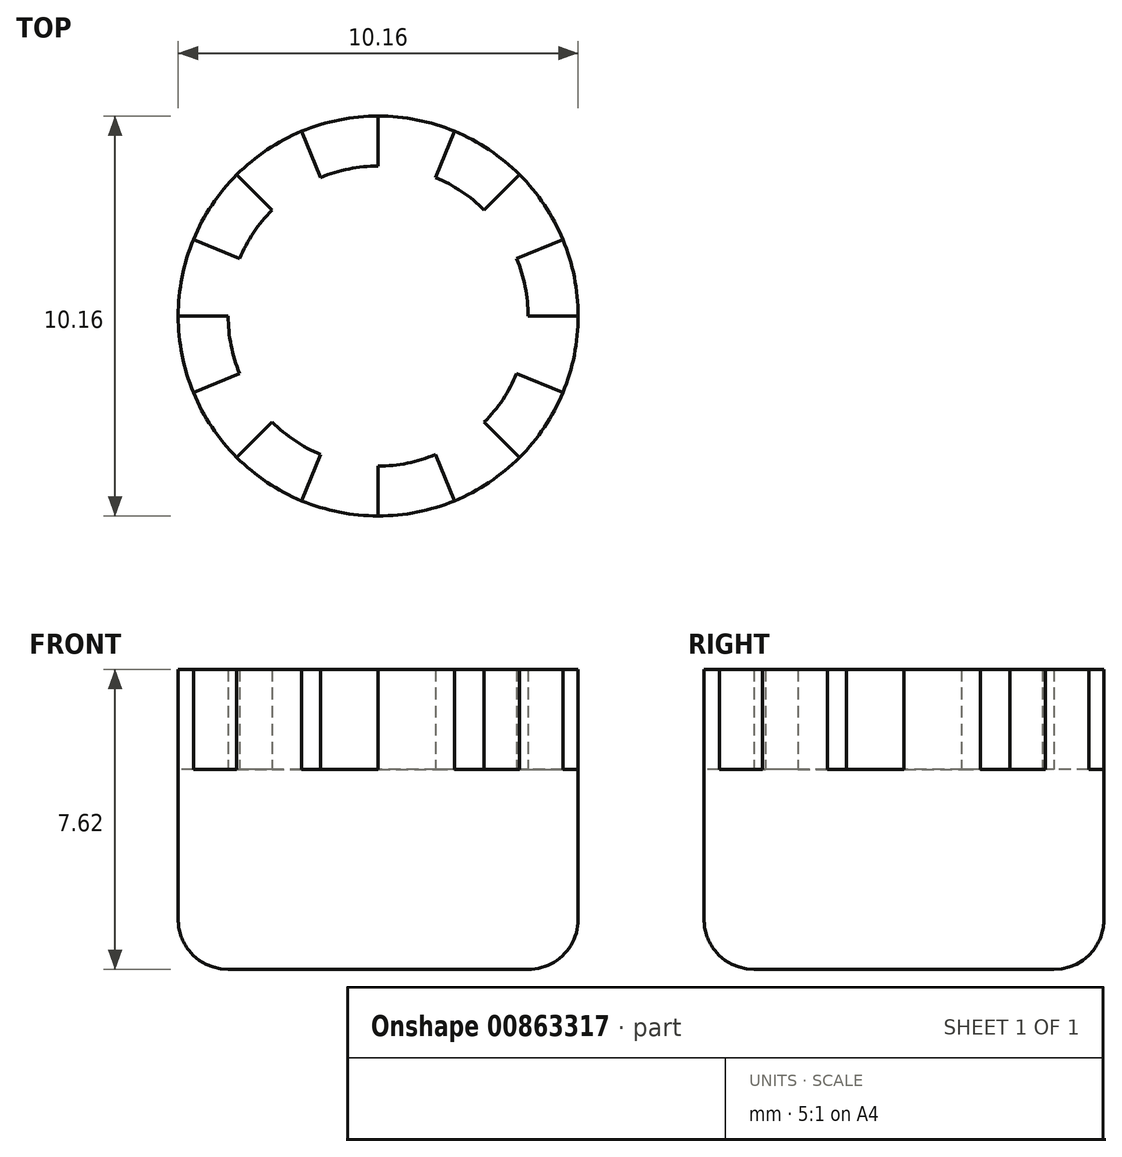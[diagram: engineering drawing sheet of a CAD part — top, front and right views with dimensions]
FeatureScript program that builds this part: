
annotation { "Feature Type Name" : "Feature", "Feature Type Description" : "" }
export const myFeature = defineFeature(function(context is Context, id is Id, definition is map)
    precondition{}
    {
        {
            var Q0;
            Q0=qCreatedBy(makeId("Top.planeOp"),FACE);
            var sketch = newSketch(context, id + "F0", { "sketchPlane" : qUnion([Q0])});
            skCircle(sketch, "E0", {"center": v(0, 0) * mm, "radius": 5.08 * mm});
            skArc(sketch, "E1", {"start": v(0, 3.81) * mm, "mid": v(-0.74, 3.74) * mm, "end": v(-1.46, 3.52) * mm});
            skLineSegment(sketch, "E2", {"start": v(-5.08, 0) * mm, "end": v(-3.81, 0) * mm});
            skLineSegment(sketch, "E3", {"start": v(0, 5.08) * mm, "end": v(0, 3.81) * mm});
            skLineSegment(sketch, "E4", {"start": v(-3.6, 3.6) * mm, "end": v(-2.7, 2.7) * mm});
            skLineSegment(sketch, "E5", {"start": v(2.7, -2.7) * mm, "end": v(3.6, -3.6) * mm});
            skLineSegment(sketch, "E6", {"start": v(-1.94, 4.7) * mm, "end": v(-1.46, 3.52) * mm});
            skLineSegment(sketch, "E7", {"start": v(1.46, -3.52) * mm, "end": v(1.94, -4.7) * mm});
            skLineSegment(sketch, "E8", {"start": v(-3.52, 1.46) * mm, "end": v(-4.7, 1.94) * mm});
            skLineSegment(sketch, "E9", {"start": v(3.52, -1.46) * mm, "end": v(4.7, -1.94) * mm});
            skLineSegment(sketch, "E10", {"start": v(1.46, 3.52) * mm, "end": v(1.94, 4.7) * mm});
            skLineSegment(sketch, "E11", {"start": v(2.7, 2.7) * mm, "end": v(3.6, 3.6) * mm});
            skLineSegment(sketch, "E12", {"start": v(3.52, 1.46) * mm, "end": v(4.7, 1.94) * mm});
            skLineSegment(sketch, "E13", {"start": v(-2.7, -2.7) * mm, "end": v(-3.6, -3.6) * mm});
            skLineSegment(sketch, "E14", {"start": v(-3.52, -1.46) * mm, "end": v(-4.7, -1.94) * mm});
            skLineSegment(sketch, "E15", {"start": v(-1.46, -3.52) * mm, "end": v(-1.94, -4.7) * mm});
            skLineSegment(sketch, "E16.trimOffspring", {"start": v(0, -3.81) * mm, "end": v(0, -5.08) * mm});
            skLineSegment(sketch, "E17.trimOffspring", {"start": v(3.81, 0) * mm, "end": v(5.08, 0) * mm});
            skArc(sketch, "E18.trimOffspring", {"start": v(-2.7, 2.7) * mm, "mid": v(-3.17, 2.12) * mm, "end": v(-3.52, 1.46) * mm});
            skArc(sketch, "E19.trimOffspring", {"start": v(2.7, 2.7) * mm, "mid": v(2.12, 3.17) * mm, "end": v(1.46, 3.52) * mm});
            skArc(sketch, "E20.trimOffspring", {"start": v(3.81, 0) * mm, "mid": v(3.74, 0.74) * mm, "end": v(3.52, 1.46) * mm});
            skArc(sketch, "E21.trimOffspring", {"start": v(2.7, -2.7) * mm, "mid": v(3.17, -2.12) * mm, "end": v(3.52, -1.46) * mm});
            skArc(sketch, "E22.trimOffspring", {"start": v(0, -3.81) * mm, "mid": v(0.74, -3.74) * mm, "end": v(1.46, -3.52) * mm});
            skArc(sketch, "E23.trimOffspring", {"start": v(-2.7, -2.7) * mm, "mid": v(-2.12, -3.17) * mm, "end": v(-1.46, -3.52) * mm});
            skArc(sketch, "E24.trimOffspring", {"start": v(-3.81, 0) * mm, "mid": v(-3.74, -0.74) * mm, "end": v(-3.52, -1.46) * mm});
            skSolve(sketch);
        }
        {
            var Q0;
            Q0=makeQuery(id+"F0.imprint","IMPRINT",FACE,{"disambiguationData":[TD([[makeQuery(id+"F0.imprint","IMPRINT",EDGE,{"derivedFrom":sQuery(id+"F0.wireOp",EDGE,"E1")}),1.0]])]});
            extrude(context, id + "F1", {"entities" : qUnion([Q0]), "depth" : 5.08 * mm, "offsetDistance" : 25.4 * mm});
        }
        {
            var Q0;
            Q0=makeQuery(id+"F0.imprint","IMPRINT",FACE,{"disambiguationData":[TD([[makeQuery(id+"F0.imprint","IMPRINT",EDGE,{"derivedFrom":sQuery(id+"F0.wireOp",EDGE,"E1")}),-1.0]])]});
            var Q1;
            {var subQ0=sQuery(id+"F0.wireOp",EDGE,"E10");Q1=makeQuery(id+"F0.imprint","IMPRINT",FACE,{"disambiguationData":[TD([[makeQuery(id+"F0.imprint","IMPRINT",EDGE,{"derivedFrom":subQ0}),-1.0]])]});}
            var Q2;
            {var subQ0=sQuery(id+"F0.wireOp",EDGE,"E12");Q2=makeQuery(id+"F0.imprint","IMPRINT",FACE,{"disambiguationData":[TD([[makeQuery(id+"F0.imprint","IMPRINT",EDGE,{"derivedFrom":subQ0}),-1.0]])]});}
            var Q3;
            {var subQ0=sQuery(id+"F0.wireOp",EDGE,"E4");Q3=makeQuery(id+"F0.imprint","IMPRINT",FACE,{"disambiguationData":[TD([[makeQuery(id+"F0.imprint","IMPRINT",EDGE,{"derivedFrom":subQ0}),-1.0]])]});}
            var Q4;
            {var subQ0=sQuery(id+"F0.wireOp",EDGE,"E2");Q4=makeQuery(id+"F0.imprint","IMPRINT",FACE,{"disambiguationData":[TD([[makeQuery(id+"F0.imprint","IMPRINT",EDGE,{"derivedFrom":subQ0}),-1.0]])]});}
            var Q5;
            {var subQ0=sQuery(id+"F0.wireOp",EDGE,"E13");Q5=makeQuery(id+"F0.imprint","IMPRINT",FACE,{"disambiguationData":[TD([[makeQuery(id+"F0.imprint","IMPRINT",EDGE,{"derivedFrom":subQ0}),1.0]])]});}
            var Q6;
            {var subQ0=sQuery(id+"F0.wireOp",EDGE,"E7");Q6=makeQuery(id+"F0.imprint","IMPRINT",FACE,{"disambiguationData":[TD([[makeQuery(id+"F0.imprint","IMPRINT",EDGE,{"derivedFrom":subQ0}),-1.0]])]});}
            var Q7;
            {var subQ0=sQuery(id+"F0.wireOp",EDGE,"E5");Q7=makeQuery(id+"F0.imprint","IMPRINT",FACE,{"disambiguationData":[TD([[makeQuery(id+"F0.imprint","IMPRINT",EDGE,{"derivedFrom":subQ0}),1.0]])]});}
            extrude(context, id + "F2", {"entities" : qUnion([Q0, Q1, Q2, Q3, Q4, Q5, Q6, Q7]), "operationType" : NewBodyOperationType.ADD, "depth" : 7.62 * mm, "offsetDistance" : 25.4 * mm});
        }
        {
            var Q0;
            {var subQ0=sQuery(id+"F0.wireOp",EDGE,"E0");var subQ1=makeQuery(id+"F0.imprint","INTERSECT",VERTEX,{"derivedFrom":[subQ0,sQuery(id+"F0.wireOp",EDGE,"E5")]});var subQ2=makeQuery(id+"F0.imprint","INTERSECT",VERTEX,{"derivedFrom":[subQ0,sQuery(id+"F0.wireOp",EDGE,"E9")]});var subQ3=makeQuery(id+"F0.imprint","INTERSECT",VERTEX,{"derivedFrom":[subQ0,sQuery(id+"F0.wireOp",EDGE,"E7")]});var subQ5=makeQuery(id+"F0.imprint","INTERSECT",VERTEX,{"derivedFrom":[subQ0,sQuery(id+"F0.wireOp",EDGE,"E13")]});var subQ6=makeQuery(id+"F0.imprint","INTERSECT",VERTEX,{"derivedFrom":[subQ0,sQuery(id+"F0.wireOp",EDGE,"E15")]});var subQ7=makeQuery(id+"F0.imprint","INTERSECT",VERTEX,{"derivedFrom":[subQ0,sQuery(id+"F0.wireOp",EDGE,"E2")]});var subQ9=makeQuery(id+"F0.imprint","INTERSECT",VERTEX,{"derivedFrom":[subQ0,sQuery(id+"F0.wireOp",EDGE,"E4")]});var subQ11=makeQuery(id+"F0.imprint","INTERSECT",VERTEX,{"derivedFrom":[subQ0,sQuery(id+"F0.wireOp",EDGE,"E3")]});var subQ13=makeQuery(id+"F0.imprint","INTERSECT",VERTEX,{"derivedFrom":[subQ0,sQuery(id+"F0.wireOp",EDGE,"E10")]});var subQ14=makeQuery(id+"F0.imprint","INTERSECT",VERTEX,{"derivedFrom":[subQ0,sQuery(id+"F0.wireOp",EDGE,"E11")]});var subQ15=makeQuery(id+"F0.imprint","INTERSECT",VERTEX,{"derivedFrom":[subQ0,sQuery(id+"F0.wireOp",EDGE,"E12")]});Q0=makeQuery(id+"F2.boolean.opBoolean","MERGE",EDGE,{"derivedFrom":[makeQuery(id+"F1.opExtrude","CAP_EDGE",EDGE,{"disambiguationData":[OSD([subQ0]),TDD([makeQuery(id+"F0.imprint","IMPRINT",EDGE,{"disambiguationData":[TD([[subQ14,1.0]])],"derivedFrom":subQ0})])],"isStart":true}),makeQuery(id+"F1.opExtrude","CAP_EDGE",EDGE,{"disambiguationData":[OSD([subQ0]),TDD([makeQuery(id+"F0.imprint","IMPRINT",EDGE,{"disambiguationData":[TD([[subQ11,1.0]])],"derivedFrom":subQ0})])],"isStart":true}),makeQuery(id+"F1.opExtrude","CAP_EDGE",EDGE,{"disambiguationData":[OSD([subQ0]),TDD([makeQuery(id+"F0.imprint","IMPRINT",EDGE,{"disambiguationData":[TD([[subQ9,1.0]])],"derivedFrom":subQ0})])],"isStart":true}),makeQuery(id+"F1.opExtrude","CAP_EDGE",EDGE,{"disambiguationData":[OSD([subQ0]),TDD([makeQuery(id+"F0.imprint","IMPRINT",EDGE,{"disambiguationData":[TD([[subQ7,1.0]])],"derivedFrom":subQ0})])],"isStart":true}),makeQuery(id+"F1.opExtrude","CAP_EDGE",EDGE,{"disambiguationData":[OSD([subQ0]),TDD([makeQuery(id+"F0.imprint","IMPRINT",EDGE,{"disambiguationData":[TD([[subQ5,1.0]])],"derivedFrom":subQ0})])],"isStart":true}),makeQuery(id+"F1.opExtrude","CAP_EDGE",EDGE,{"disambiguationData":[OSD([subQ0]),TDD([makeQuery(id+"F0.imprint","IMPRINT",EDGE,{"disambiguationData":[TD([[subQ6,-1.0]])],"derivedFrom":subQ0})])],"isStart":true}),makeQuery(id+"F1.opExtrude","CAP_EDGE",EDGE,{"disambiguationData":[OSD([subQ0]),TDD([makeQuery(id+"F0.imprint","IMPRINT",EDGE,{"disambiguationData":[TD([[subQ1,1.0]])],"derivedFrom":subQ0})])],"isStart":true}),makeQuery(id+"F1.opExtrude","CAP_EDGE",EDGE,{"disambiguationData":[OSD([subQ0]),TDD([makeQuery(id+"F0.imprint","IMPRINT",EDGE,{"disambiguationData":[TD([[subQ2,-1.0]])],"derivedFrom":subQ0})])],"isStart":true}),makeQuery(id+"F2.opExtrude","CAP_EDGE",EDGE,{"disambiguationData":[OSD([subQ0]),TDD([makeQuery(id+"F0.imprint","IMPRINT",EDGE,{"disambiguationData":[TD([[subQ15,1.0]])],"derivedFrom":subQ0})])],"isStart":true}),makeQuery(id+"F2.opExtrude","CAP_EDGE",EDGE,{"disambiguationData":[OSD([subQ0]),TDD([makeQuery(id+"F0.imprint","IMPRINT",EDGE,{"disambiguationData":[TD([[subQ13,1.0]])],"derivedFrom":subQ0})])],"isStart":true}),makeQuery(id+"F2.opExtrude","CAP_EDGE",EDGE,{"disambiguationData":[OSD([subQ0]),TDD([makeQuery(id+"F0.imprint","IMPRINT",EDGE,{"disambiguationData":[TD([[subQ11,-1.0]])],"derivedFrom":subQ0})])],"isStart":true}),makeQuery(id+"F2.opExtrude","CAP_EDGE",EDGE,{"disambiguationData":[OSD([subQ0]),TDD([makeQuery(id+"F0.imprint","IMPRINT",EDGE,{"disambiguationData":[TD([[subQ9,-1.0]])],"derivedFrom":subQ0})])],"isStart":true}),makeQuery(id+"F2.opExtrude","CAP_EDGE",EDGE,{"disambiguationData":[OSD([subQ0]),TDD([makeQuery(id+"F0.imprint","IMPRINT",EDGE,{"disambiguationData":[TD([[subQ7,-1.0]])],"derivedFrom":subQ0})])],"isStart":true}),makeQuery(id+"F2.opExtrude","CAP_EDGE",EDGE,{"disambiguationData":[OSD([subQ0]),TDD([makeQuery(id+"F0.imprint","IMPRINT",EDGE,{"disambiguationData":[TD([[subQ5,-1.0]])],"derivedFrom":subQ0})])],"isStart":true}),makeQuery(id+"F2.opExtrude","CAP_EDGE",EDGE,{"disambiguationData":[OSD([subQ0]),TDD([makeQuery(id+"F0.imprint","IMPRINT",EDGE,{"disambiguationData":[TD([[subQ3,1.0]])],"derivedFrom":subQ0})])],"isStart":true}),makeQuery(id+"F2.opExtrude","CAP_EDGE",EDGE,{"disambiguationData":[OSD([subQ0]),TDD([makeQuery(id+"F0.imprint","IMPRINT",EDGE,{"disambiguationData":[TD([[subQ1,-1.0]])],"derivedFrom":subQ0})])],"isStart":true})]});}
            fillet(context, id + "F3", {"entities" : qUnion([Q0]), "radius" : 1.27 * mm, "tangentPropagation" : true, "allowEdgeOverflow" : false});
        }
    });
